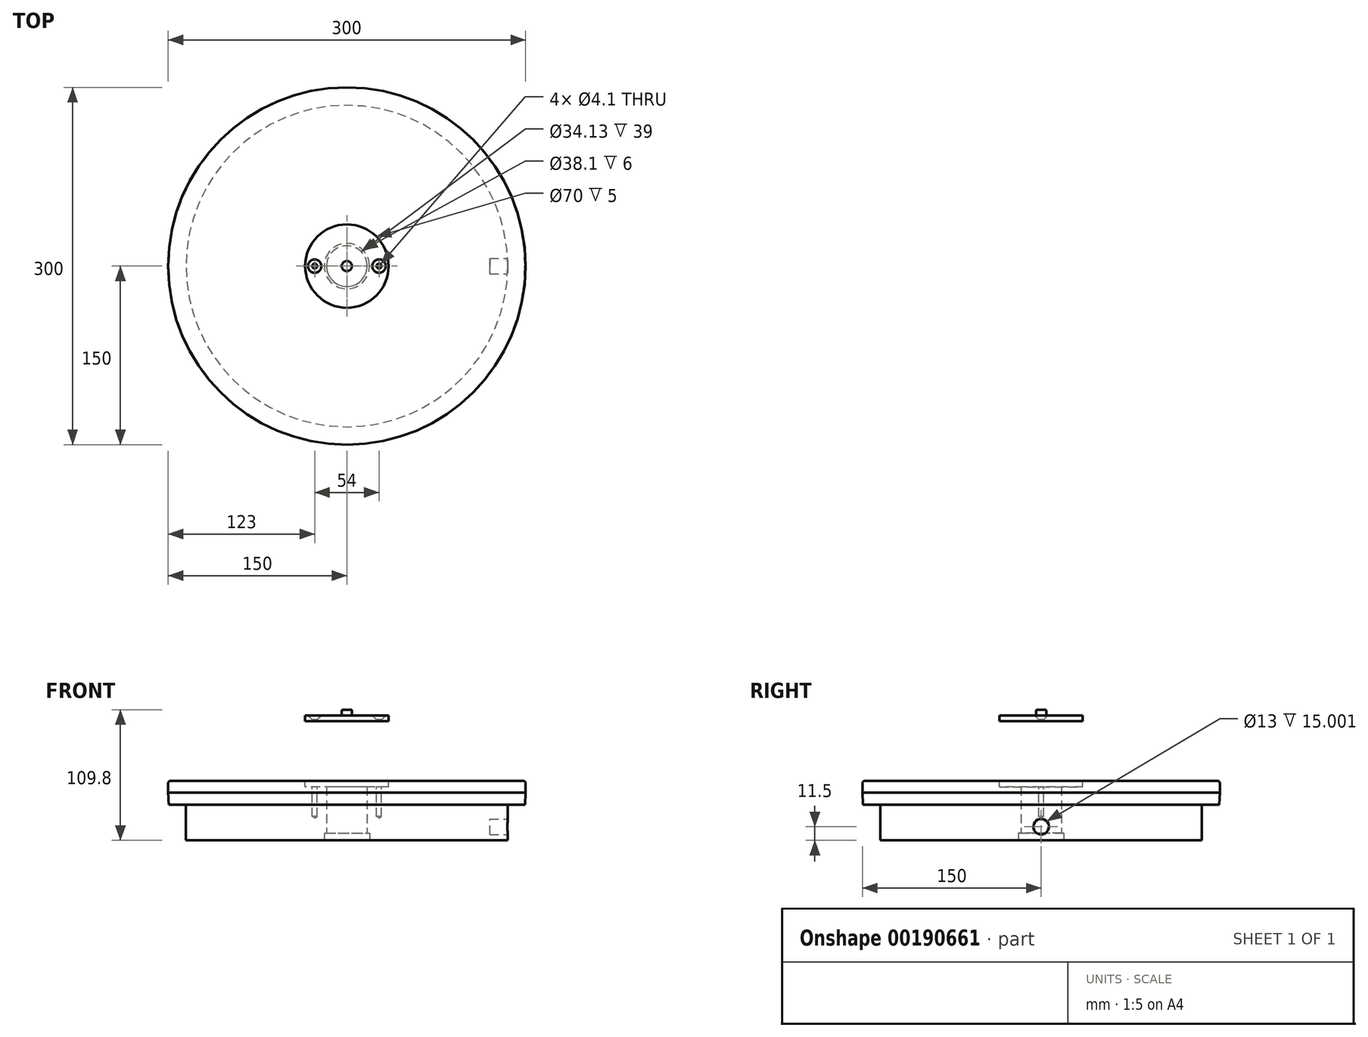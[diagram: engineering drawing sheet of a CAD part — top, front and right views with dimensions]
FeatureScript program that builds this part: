
annotation { "Feature Type Name" : "Feature", "Feature Type Description" : "" }
export const myFeature = defineFeature(function(context is Context, id is Id, definition is map)
    precondition{}
    {
        {
            var Q0;
            Q0=qCreatedBy(makeId("Right.planeOp"),FACE);
            var sketch = newSketch(context, id + "F0", { "sketchPlane" : qUnion([Q0])});
            skLineSegment(sketch, "E0", {"start": v(0, 20) * mm, "end": v(150, 20) * mm});
            skLineSegment(sketch, "E1", {"start": v(150, 20) * mm, "end": v(150, 10) * mm});
            skLineSegment(sketch, "E2", {"start": v(149.5, 0) * mm, "end": v(135, 0) * mm});
            skLineSegment(sketch, "E3", {"start": v(135, 0) * mm, "end": v(135, -30) * mm});
            skLineSegment(sketch, "E4", {"start": v(135, -30) * mm, "end": v(0, -30) * mm});
            skLineSegment(sketch, "E5", {"start": v(0, -30) * mm, "end": v(0, 20) * mm});
            skLineSegment(sketch, "E6", {"start": v(150, 10) * mm, "end": v(149.5, 0) * mm});
            skPoint(sketch, "E7.orphan", {"position": v(150, 0) * mm});
            skSolve(sketch);
        }
        {
            var Q0;
            Q0 = qSketchRegion(id + "F0", true);
            var Q1;
            Q1=sQuery(id+"F0.wireOp",EDGE,"E5");
            revolve(context, id + "F1", {"entities" : qUnion([Q0]), "axis" : qUnion([Q1]), "revolveType" : RevolveType.FULL});
        }
        {
            var Q0;
            Q0=makeQuery(id+"F1.opRevolve","SWEPT_FACE",FACE,{"disambiguationData":[OSD([sQuery(id+"F0.wireOp",EDGE,"E4")])]});
            var sketch = newSketch(context, id + "F2", { "sketchPlane" : qUnion([Q0])});
            skPoint(sketch, "E8", {"position": v(0, 0) * mm});
            skSolve(sketch);
        }
        {
            var Q0;
            Q0=sQuery(id+"F2.wireOp",VERTEX,"E8");
            var Q1;
            Q1=makeQuery(id+"F1.opRevolve","SWEPT_BODY",BODY,{"disambiguationData":[OSD([sQuery(id+"F0.wireOp",EDGE,"E0"),sQuery(id+"F0.wireOp",EDGE,"E1"),sQuery(id+"F0.wireOp",EDGE,"E2"),sQuery(id+"F0.wireOp",EDGE,"E3"),sQuery(id+"F0.wireOp",EDGE,"E4"),sQuery(id+"F0.wireOp",EDGE,"E5")])]});
            hole(context, id + "F3", {"style" : HoleStyle.C_BORE, "endStyle" : HoleEndStyle.THROUGH, "standardTappedOrClearance" : lookupTablePath({ "standard" : "ANSI", "engagement" : "75%", "pitch" : "6 tpi", "size" : "1 1/2", "type" : "Tapped" }), "standardBlindInLast" : lookupTablePath({ "standard" : "ANSI", "engagement" : "75%", "pitch" : "6 tpi", "size" : "1 1/2", "type" : "Tapped" }), "holeDiameter" : 34.13 * mm, "cBoreDiameter" : 38.1 * mm, "cBoreDepth" : 6 * mm, "startFromSketch" : true, "locations" : qUnion([Q0]), "scope" : qUnion([Q1]), "isTappedThrough" : true, "majorDiameter" : 38.1 * mm, "showTappedDepth" : true});
        }
        {
            var Q0;
            Q0=makeQuery(id+"F1.opRevolve","SWEPT_FACE",FACE,{"disambiguationData":[OSD([sQuery(id+"F0.wireOp",EDGE,"E4")])]});
            var sketch = newSketch(context, id + "F4", { "sketchPlane" : qUnion([Q0])});
            skLineSegment(sketch, "E9", {"start": v(0, 0) * mm, "end": v(135, 0) * mm, "construction": true});
            skSolve(sketch);
        }
        {
            var Q0;
            Q0=sQuery(id+"F4.wireOp",EDGE,"E9");
            var Q1;
            Q1=sQuery(id+"F4.wireOp",VERTEX,"E9.end");
            cPlane(context, id + "F5", {"entities" : qUnion([Q0, Q1]), "cplaneType" : CPlaneType.LINE_POINT, "offset" : 25 * mm, "width" : 150 * mm, "height" : 150 * mm});
        }
        {
            var Q0;
            Q0=qCreatedBy(id+"F5.planeOp",FACE);
            var sketch = newSketch(context, id + "F6", { "sketchPlane" : qUnion([Q0])});
            skLineSegment(sketch, "E10", {"start": v(0, -37) * mm, "end": v(0, 0) * mm, "construction": true});
            skCircle(sketch, "E11", {"center": v(0, -18.5) * mm, "radius": 6.5 * mm});
            skLineSegment(sketch, "E12.0", {"start": v(135, -30) * mm, "end": v(-135, -30) * mm, "construction": true});
            skSolve(sketch);
        }
        {
            var Q0;
            Q0 = qSketchRegion(id + "F6", true);
            extrude(context, id + "F7", {"entities" : qUnion([Q0]), "operationType" : NewBodyOperationType.REMOVE, "oppositeDirection" : true, "depth" : 15 * mm});
        }
        {
            var Q0;
            Q0=makeQuery(id+"F1.opRevolve","SWEPT_EDGE",EDGE,{"disambiguationData":[OSD([sQuery(id+"F0.wireOp",EDGE,"E0"),sQuery(id+"F0.wireOp",EDGE,"E1")])]});
            fillet(context, id + "F8", {"entities" : qUnion([Q0]), "radius" : 2 * mm, "tangentPropagation" : true, "allowEdgeOverflow" : false});
        }
        {
            var Q0;
            Q0=makeQuery(id+"F1.opRevolve","SWEPT_FACE",FACE,{"disambiguationData":[OSD([sQuery(id+"F0.wireOp",EDGE,"E0")])]});
            cPlane(context, id + "F9", {"entities" : qUnion([Q0]), "cplaneType" : CPlaneType.OFFSET, "offset" : 0 * mm, "width" : 150 * mm, "height" : 150 * mm});
        }
        {
            var Q0;
            Q0=qCreatedBy(id+"F9.planeOp",FACE);
            var sketch = newSketch(context, id + "F10", { "sketchPlane" : qUnion([Q0])});
            skPoint(sketch, "E13.0", {"position": v(0, 0) * mm});
            skCircle(sketch, "E14", {"center": v(0, 0) * mm, "radius": 35 * mm});
            skSolve(sketch);
        }
        {
            var Q0;
            Q0 = qSketchRegion(id + "F10", true);
            extrude(context, id + "F11", {"entities" : qUnion([Q0]), "operationType" : NewBodyOperationType.REMOVE, "oppositeDirection" : true, "depth" : 5 * mm});
        }
        {
            var Q0;
            Q0=qCreatedBy(id+"F9.planeOp",FACE);
            cPlane(context, id + "F12", {"entities" : qUnion([Q0]), "cplaneType" : CPlaneType.OFFSET, "offset" : 50 * mm, "width" : 150 * mm, "height" : 150 * mm});
        }
        {
            var Q0;
            Q0=qCreatedBy(id+"F12.planeOp",FACE);
            var sketch = newSketch(context, id + "F13", { "sketchPlane" : qUnion([Q0])});
            skCircle(sketch, "E15.0", {"center": v(0, 0) * mm, "radius": 35 * mm});
            skLineSegment(sketch, "E16.0", {"start": v(0, 0) * mm, "end": v(135, 0) * mm, "construction": true});
            skSolve(sketch);
        }
        {
            var Q0;
            Q0 = qSketchRegion(id + "F13", true);
            var Q1;
            Q1 = qConstructionFilter(qBodyType(qCreatedBy(id + "F13" ,EDGE), BodyType.WIRE), ConstructionObject.NO);
            extrude(context, id + "F14", {"entities" : qUnion([Q0]), "surfaceEntities" : qUnion([Q1]), "depth" : 4.8 * mm});
        }
        {
            var Q0;
            Q0=makeQuery(id+"F14.opExtrude","CAP_FACE",FACE,{"disambiguationData":[OSD([sQuery(id+"F13.wireOp",EDGE,"E15.0")])],"isStart":false});
            var sketch = newSketch(context, id + "F15", { "sketchPlane" : qUnion([Q0])});
            skCircle(sketch, "E17", {"center": v(0, 0) * mm, "radius": 4.25 * mm});
            skCircle(sketch, "E18.0", {"center": v(0, 0) * mm, "radius": 19.05 * mm, "construction": true});
            skSolve(sketch);
        }
        {
            var Q0;
            Q0 = qSketchRegion(id + "F15", true);
            extrude(context, id + "F16", {"entities" : qUnion([Q0]), "operationType" : NewBodyOperationType.ADD, "depth" : 5 * mm});
        }
        {
            var Q0;
            Q0=makeQuery(id+"F14.opExtrude","CAP_FACE",FACE,{"disambiguationData":[OSD([sQuery(id+"F13.wireOp",EDGE,"E15.0")])],"isStart":false});
            var sketch = newSketch(context, id + "F17", { "sketchPlane" : qUnion([Q0])});
            skLineSegment(sketch, "E19", {"start": v(35, 0) * mm, "end": v(-35, 0) * mm, "construction": true});
            skPoint(sketch, "E20", {"position": v(-27, 0) * mm});
            skPoint(sketch, "E21", {"position": v(27, 0) * mm});
            skSolve(sketch);
        }
        {
            var Q0;
            Q0=makeQuery(id+"F11.boolean.opBoolean","COPY",FACE,{"derivedFrom":makeQuery(id+"F11.opExtrude","CAP_FACE",FACE,{"disambiguationData":[OSD([sQuery(id+"F10.wireOp",EDGE,"E14")])],"isStart":false})});
            var sketch = newSketch(context, id + "F18", { "sketchPlane" : qUnion([Q0])});
            skPoint(sketch, "E22.0", {"position": v(-27, 0) * mm});
            skPoint(sketch, "E23.0", {"position": v(27, 0) * mm});
            skSolve(sketch);
        }
        {
            var Q0;
            Q0=sQuery(id+"F17.wireOp",VERTEX,"E20");
            var Q1;
            Q1=sQuery(id+"F17.wireOp",VERTEX,"E21");
            var Q2;
            Q2=makeQuery(id+"F14.opExtrude","SWEPT_BODY",BODY,{"disambiguationData":[OSD([sQuery(id+"F13.wireOp",EDGE,"E15.0")])]});
            hole(context, id + "F19", {"style" : HoleStyle.C_SINK, "endStyle" : HoleEndStyle.BLIND, "standardTappedOrClearance" : lookupTablePath({ "standard" : "ISO", "engagement" : "75%", "pitch" : "0.9 mm", "size" : "M5", "type" : "Tapped" }), "standardBlindInLast" : lookupTablePath({ "standard" : "ISO", "engagement" : "75%", "pitch" : "0.9 mm", "size" : "M5", "type" : "Tapped" }), "holeDiameter" : 4.1 * mm, "cSinkDiameter" : 11.2 * mm, "cSinkAngle" : 90 * degree, "holeDepth" : 25 * mm, "startFromSketch" : true, "locations" : qUnion([Q0, Q1]), "scope" : qUnion([Q2])});
        }
        {
            var Q0;
            Q0=sQuery(id+"F18.wireOp",VERTEX,"E22.0");
            var Q1;
            Q1=sQuery(id+"F18.wireOp",VERTEX,"E23.0");
            var Q2;
            Q2=makeQuery(id+"F1.opRevolve","SWEPT_BODY",BODY,{"disambiguationData":[OSD([sQuery(id+"F0.wireOp",EDGE,"E0"),sQuery(id+"F0.wireOp",EDGE,"E1"),sQuery(id+"F0.wireOp",EDGE,"E2"),sQuery(id+"F0.wireOp",EDGE,"E3"),sQuery(id+"F0.wireOp",EDGE,"E4"),sQuery(id+"F0.wireOp",EDGE,"E5")])]});
            hole(context, id + "F20", {"style" : HoleStyle.SIMPLE, "endStyle" : HoleEndStyle.BLIND, "standardTappedOrClearance" : lookupTablePath({ "standard" : "ISO", "engagement" : "75%", "pitch" : "0.9 mm", "size" : "M5", "type" : "Tapped" }), "standardBlindInLast" : lookupTablePath({ "standard" : "ISO", "engagement" : "75%", "pitch" : "0.9 mm", "size" : "M5", "type" : "Tapped" }), "holeDiameter" : 4.1 * mm, "holeDepth" : 25 * mm, "startFromSketch" : true, "locations" : qUnion([Q0, Q1]), "scope" : qUnion([Q2])});
        }
        {
            var Q0;
            Q0=makeQuery(id+"F16.opExtrude","CAP_EDGE",EDGE,{"disambiguationData":[OSD([sQuery(id+"F15.wireOp",EDGE,"E17")])],"isStart":false});
            fillet(context, id + "F21", {"entities" : qUnion([Q0]), "radius" : 1 * mm, "tangentPropagation" : true, "allowEdgeOverflow" : false});
        }
    });
